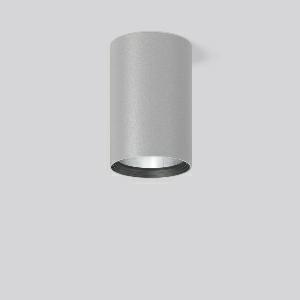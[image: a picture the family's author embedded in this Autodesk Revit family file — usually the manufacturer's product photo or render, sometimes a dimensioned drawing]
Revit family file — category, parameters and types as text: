
# Revit family: heledon_maxi_a_931217_004_1f2e
name_source: partatom
category: Lighting Fixtures
units: mm (PartAtom-declared; Revit-internal decimal feet)

## family parameters
Cut with Voids When Loaded = No
Host = Face
Light Source = No
Part Type = Normal
Room Calculation Point = No
Round Connector Dimension = Use Diameter
Shared = No

## types (1)
- HELEDON maxi A (1 x LED Modul 930, 3350 lm, 3000)
    Apparent Load = 25 VA
    Approval mark = CE
    CIE Flux Codes = 100 100 100 100 100
    Color Rendering = 90
    Color Temperature = 3000
    Default Elevation = 1800 mm
    Description = Series: HELEDON maxi
Cylindrical surface-mounted downlight. Housing: die-cast aluminium, powder-coated. Internal ceiling frame polycarbonate with bayonet mounting. Black plastic ring and recessed LED to prevent glare from the side. Optical assembly with reflector made of MIRO-Silver with 98% total light reflection for outstanding efficiency - can be changed without tools. Best colour rendering index Ra>90. Suitable for Ceiling mounting. Easy installation with a separate ceiling frame with bayonet mounting and plug connection. Driver integrated. Connected via plug-in connector. High quality converter without flickering and stroboscopic effect. The following accessories can be mounted without use of tools: interchangeable lenses, decorative glasses, honeycomb louvre, clear and frosted diffusers, white interchangeable plastic ring. 
Colour: silver
Diameter: 123 mm
Height: 183 mm
Lamp: LED
Socket: without socket
Colour temperature: 3000K
Colour rendering index (CRI): 92
System power: 25 W
Rated luminous flux: 3350 lm
Luminous efficiency: 134 lm/W
Control gear: Regulated power supply
Protection class: I
Type of protection: IP 20
    Height = 183 mm
    Lamp = 1 x LED Modul 930
    Lamp Light Flux = 3350 lm
    Lamp count = 1
    Length = 123 mm
    Lifetime = 50000 h
    Luminous efficacy = 134 lm/W
    Manufacturer = RZB
    ModVariant = No
    Model = 931217.004
    Mounting Place = Ceiling
    Mounting Type = Surface mounted
    Number of Poles = 1
    OnlyDefault = Yes
    Power Factor = 1
    Product Name = HELEDON maxi A
    Product group = Surface mounted downlights
    ProductGroupID = 302
    Protection Class = Protection class I
    Protection Degree = IP 20
    RLX_Detail_Level = 1
    RLX_Emergency_Light_Flux = 0 lm
    RLX_Emergency_Type = 0
    RLX_Emergency_Type_DB = No
    RlxData = <blob elided: 100525 chars, md5=f5ec70cf>
    Socket = socket
    Standby Power = 0 W
    System Light Flux = 3350 lm
    System Power = 25 W
    Type Comments = Product without accessories
    Type Image = 931192.004.jpg
    URL = http://relux.com
    VarID = ---
    Voltage = 230 V
    Voltage Range = 220-240 V
    Weight = 0.00 kg
    Width = 0 mm  [stored 0 ft]

note: [stored X ft] marks values corroborated as IEEE doubles in the binary element streams (Revit-internal decimal feet)

## geometry (parser evidence)
native form markers: Blend x4, Sweep x12
no freeform markers — native parametric forms only
